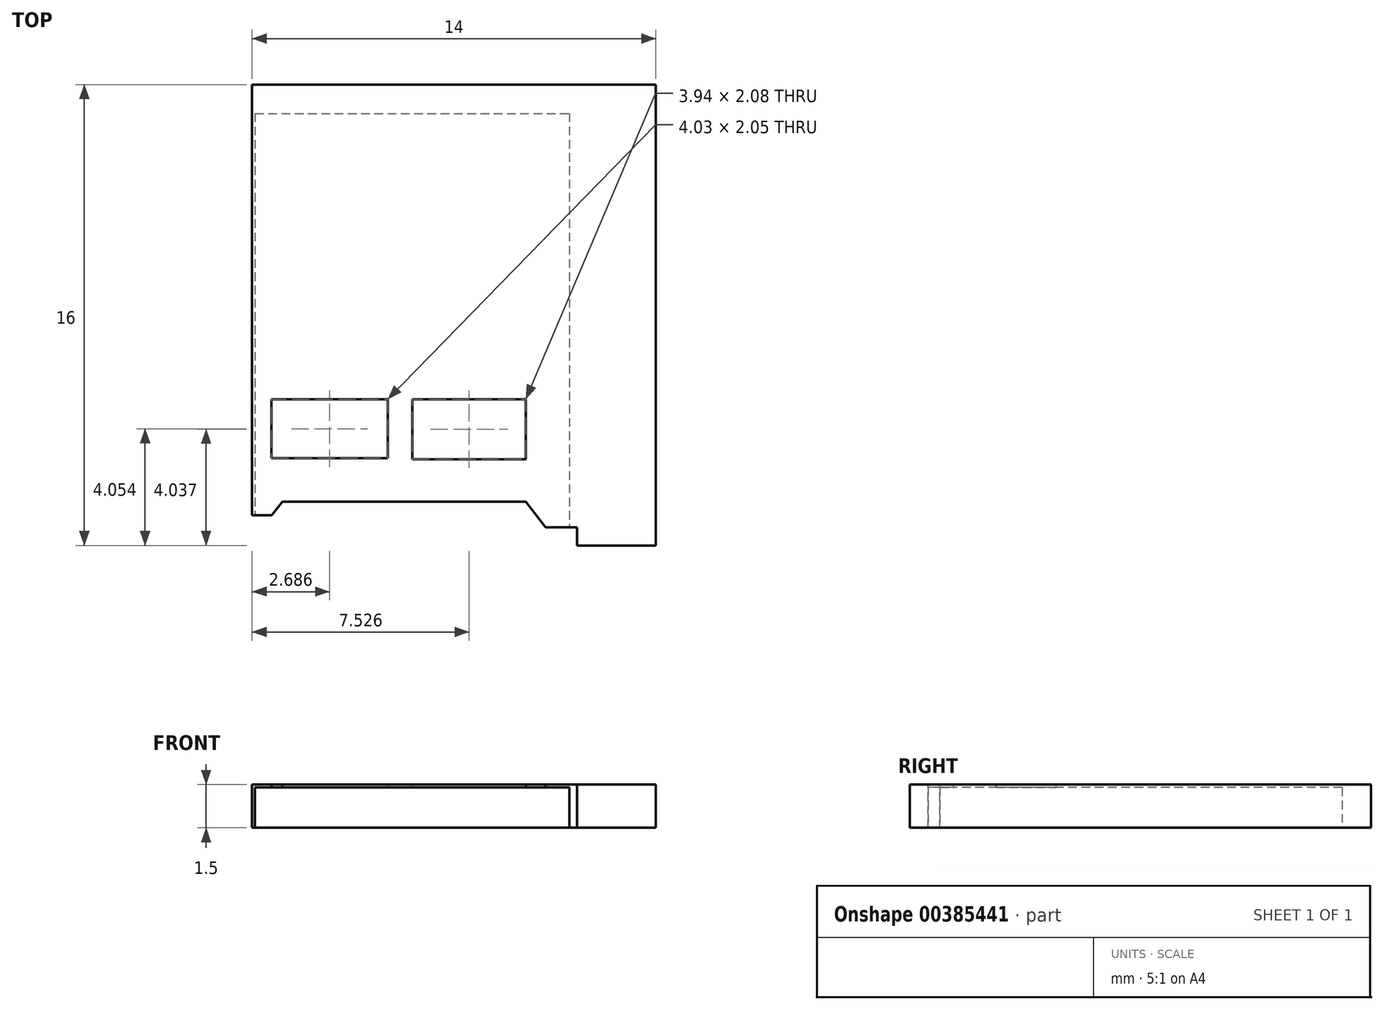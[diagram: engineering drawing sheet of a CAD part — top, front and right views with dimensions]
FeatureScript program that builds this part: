
annotation { "Feature Type Name" : "Feature", "Feature Type Description" : "" }
export const myFeature = defineFeature(function(context is Context, id is Id, definition is map)
    precondition{}
    {
        {
            var Q0;
            Q0=qCreatedBy(makeId("Top.planeOp"),FACE);
            var sketch = newSketch(context, id + "F0", { "sketchPlane" : qUnion([Q0])});
            skLineSegment(sketch, "E0.bottom", {"start": v(7, -8) * mm, "end": v(-7, -8) * mm});
            skLineSegment(sketch, "E0.top", {"start": v(7, 8) * mm, "end": v(-7, 8) * mm});
            skLineSegment(sketch, "E0.left", {"start": v(7, -8) * mm, "end": v(7, 8) * mm});
            skLineSegment(sketch, "E0.right", {"start": v(-7, -8) * mm, "end": v(-7, 8) * mm});
            skPoint(sketch, "E0.middle", {"position": v(0, 0) * mm});
            skSolve(sketch);
        }
        {
            var Q0;
            Q0=qSketchRegion(id+"F0",true);
            extrude(context, id + "F1", {"entities" : qUnion([Q0]), "depth" : 1.5 * mm});
        }
        {
            var Q0;
            Q0=makeQuery(id+"F1.opExtrude","SWEPT_FACE",FACE,{"disambiguationData":[OSD([sQuery(id+"F0.wireOp",EDGE,"E0.bottom")])]});
            var sketch = newSketch(context, id + "F2", { "sketchPlane" : qUnion([Q0])});
            skLineSegment(sketch, "E1.bottom", {"start": v(-6.9, 1.4) * mm, "end": v(4, 1.4) * mm});
            skLineSegment(sketch, "E1.top", {"start": v(-6.9, 0) * mm, "end": v(4, 0) * mm});
            skLineSegment(sketch, "E1.left", {"start": v(-6.9, 1.4) * mm, "end": v(-6.9, 0) * mm});
            skLineSegment(sketch, "E1.right", {"start": v(4, 1.4) * mm, "end": v(4, 0) * mm});
            skSolve(sketch);
        }
        {
            var Q0;
            Q0=makeQuery(id+"F2.imprint","IMPRINT",FACE,{"disambiguationData":[TD([[makeQuery(id+"F2.imprint","IMPRINT",EDGE,{"derivedFrom":sQuery(id+"F2.wireOp",EDGE,"E1.bottom")}),-1.0]])]});
            extrude(context, id + "F3", {"entities" : qUnion([Q0]), "operationType" : NewBodyOperationType.REMOVE, "oppositeDirection" : true, "depth" : 15 * mm});
        }
        {
            var Q0;
            Q0=makeQuery(id+"F1.opExtrude","CAP_FACE",FACE,{"disambiguationData":[OSD([sQuery(id+"F0.wireOp",EDGE,"E0.bottom"),sQuery(id+"F0.wireOp",EDGE,"E0.top"),sQuery(id+"F0.wireOp",EDGE,"E0.left"),sQuery(id+"F0.wireOp",EDGE,"E0.right")])],"isStart":false});
            var sketch = newSketch(context, id + "F4", { "sketchPlane" : qUnion([Q0])});
            skLineSegment(sketch, "E2", {"start": v(4.27, -8) * mm, "end": v(4.27, -7.37) * mm});
            skLineSegment(sketch, "E3", {"start": v(4.27, -7.37) * mm, "end": v(3.18, -7.37) * mm});
            skLineSegment(sketch, "E4", {"start": v(3.18, -7.37) * mm, "end": v(2.5, -6.48) * mm});
            skLineSegment(sketch, "E5", {"start": v(2.5, -6.48) * mm, "end": v(-5.95, -6.48) * mm});
            skLineSegment(sketch, "E6", {"start": v(-5.95, -6.48) * mm, "end": v(-6.32, -6.96) * mm});
            skLineSegment(sketch, "E7", {"start": v(-6.32, -6.96) * mm, "end": v(-7, -6.96) * mm});
            skLineSegment(sketch, "E8", {"start": v(-7, -6.96) * mm, "end": v(-7, -8) * mm});
            skLineSegment(sketch, "E9", {"start": v(-7, -8) * mm, "end": v(4.27, -8) * mm});
            skSolve(sketch);
        }
        {
            var Q0;
            Q0=makeQuery(id+"F4.imprint","IMPRINT",FACE,{"disambiguationData":[TD([[makeQuery(id+"F4.imprint","IMPRINT",EDGE,{"derivedFrom":sQuery(id+"F4.wireOp",EDGE,"E2")}),1.0]])]});
            extrude(context, id + "F5", {"entities" : qUnion([Q0]), "operationType" : NewBodyOperationType.REMOVE, "oppositeDirection" : true, "depth" : 25 * mm});
        }
        {
            var Q0;
            Q0=makeQuery(id+"F1.opExtrude","CAP_FACE",FACE,{"disambiguationData":[OSD([sQuery(id+"F0.wireOp",EDGE,"E0.bottom"),sQuery(id+"F0.wireOp",EDGE,"E0.top"),sQuery(id+"F0.wireOp",EDGE,"E0.left"),sQuery(id+"F0.wireOp",EDGE,"E0.right")])],"isStart":false});
            var sketch = newSketch(context, id + "F6", { "sketchPlane" : qUnion([Q0])});
            skLineSegment(sketch, "E10.bottom", {"start": v(-6.33, -4.97) * mm, "end": v(-2.3, -4.97) * mm});
            skLineSegment(sketch, "E10.top", {"start": v(-6.33, -2.92) * mm, "end": v(-2.3, -2.92) * mm});
            skLineSegment(sketch, "E10.left", {"start": v(-6.33, -4.97) * mm, "end": v(-6.33, -2.92) * mm});
            skLineSegment(sketch, "E10.right", {"start": v(-2.3, -4.97) * mm, "end": v(-2.3, -2.92) * mm});
            skLineSegment(sketch, "E11.bottom", {"start": v(-1.44, -2.92) * mm, "end": v(2.5, -2.92) * mm});
            skLineSegment(sketch, "E11.top", {"start": v(-1.44, -5) * mm, "end": v(2.5, -5) * mm});
            skLineSegment(sketch, "E11.left", {"start": v(-1.44, -2.92) * mm, "end": v(-1.44, -5) * mm});
            skLineSegment(sketch, "E11.right", {"start": v(2.5, -2.92) * mm, "end": v(2.5, -5) * mm});
            skSolve(sketch);
        }
        {
            var Q0;
            Q0=makeQuery(id+"F6.imprint","IMPRINT",FACE,{"disambiguationData":[TD([[makeQuery(id+"F6.imprint","IMPRINT",EDGE,{"derivedFrom":sQuery(id+"F6.wireOp",EDGE,"E10.bottom")}),1.0]])]});
            var Q1;
            Q1=makeQuery(id+"F6.imprint","IMPRINT",FACE,{"disambiguationData":[TD([[makeQuery(id+"F6.imprint","IMPRINT",EDGE,{"derivedFrom":sQuery(id+"F6.wireOp",EDGE,"E11.bottom")}),-1.0]])]});
            extrude(context, id + "F7", {"entities" : qUnion([Q0, Q1]), "operationType" : NewBodyOperationType.REMOVE, "oppositeDirection" : true, "depth" : 25 * mm});
        }
    });
